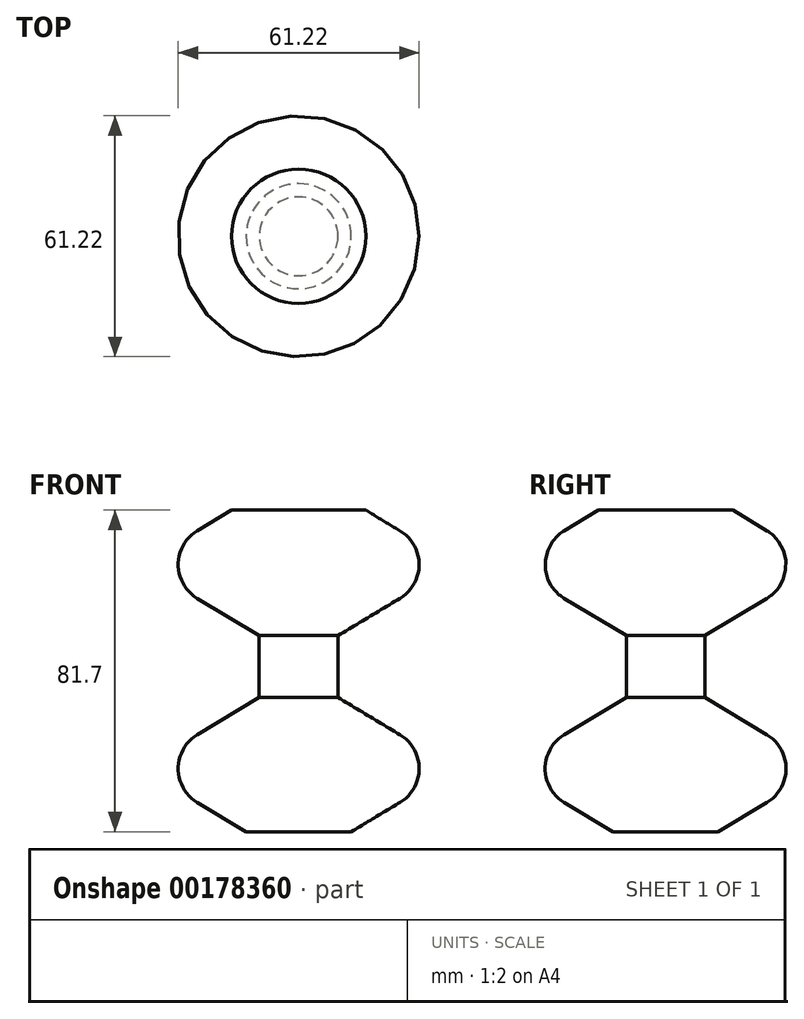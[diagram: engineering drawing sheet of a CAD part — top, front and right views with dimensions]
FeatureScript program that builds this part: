
annotation { "Feature Type Name" : "Feature", "Feature Type Description" : "" }
export const myFeature = defineFeature(function(context is Context, id is Id, definition is map)
    precondition{}
    {
        {
            var Q0;
            Q0=qCreatedBy(makeId("Front.planeOp"),FACE);
            var sketch = newSketch(context, id + "F0", { "sketchPlane" : qUnion([Q0])});
            skLineSegment(sketch, "E0", {"start": v(0, -50) * mm, "end": v(0, 50) * mm});
            skLineSegment(sketch, "E1", {"start": v(0, 63.8) * mm, "end": v(0, -60.91) * mm, "construction": true});
            skLineSegment(sketch, "E2", {"start": v(0, 50) * mm, "end": v(-40, 25.92) * mm});
            skLineSegment(sketch, "E3", {"start": v(-40, 25.92) * mm, "end": v(-10, 7.86) * mm});
            skLineSegment(sketch, "E4", {"start": v(-10, -7.86) * mm, "end": v(-40, -25.92) * mm});
            skLineSegment(sketch, "E5", {"start": v(-40, -25.92) * mm, "end": v(0, -50) * mm});
            skLineSegment(sketch, "E6", {"start": v(-10, 7.86) * mm, "end": v(-10, -7.86) * mm});
            skLineSegment(sketch, "E7", {"start": v(-13.34, -41.97) * mm, "end": v(0, -41.97) * mm});
            skLineSegment(sketch, "E8", {"start": v(-17.06, 39.73) * mm, "end": v(0, 39.73) * mm});
            skSolve(sketch);
        }
        {
            var Q0;
            {var subQ1=sQuery(id+"F0.wireOp",EDGE,"E3");Q0=makeQuery(id+"F0.imprint","IMPRINT",FACE,{"disambiguationData":[TD([[makeQuery(id+"F0.imprint","IMPRINT",EDGE,{"derivedFrom":subQ1}),1.0]])]});}
            var Q1;
            Q1=sQuery(id+"F0.wireOp",EDGE,"E1");
            revolve(context, id + "F1", {"entities" : qUnion([Q0]), "axis" : qUnion([Q1]), "revolveType" : RevolveType.FULL});
        }
        {
            var Q0;
            Q0=makeQuery(id+"F1.opRevolve","SWEPT_EDGE",EDGE,{"disambiguationData":[OSD([sQuery(id+"F0.wireOp",EDGE,"E2"),sQuery(id+"F0.wireOp",EDGE,"E3")])]});
            var Q1;
            Q1=makeQuery(id+"F1.opRevolve","SWEPT_EDGE",EDGE,{"disambiguationData":[OSD([sQuery(id+"F0.wireOp",EDGE,"E4"),sQuery(id+"F0.wireOp",EDGE,"E5")])]});
            fillet(context, id + "F2", {"entities" : qUnion([Q0, Q1]), "radius" : 10 * mm, "tangentPropagation" : true, "allowEdgeOverflow" : false});
        }
    });
